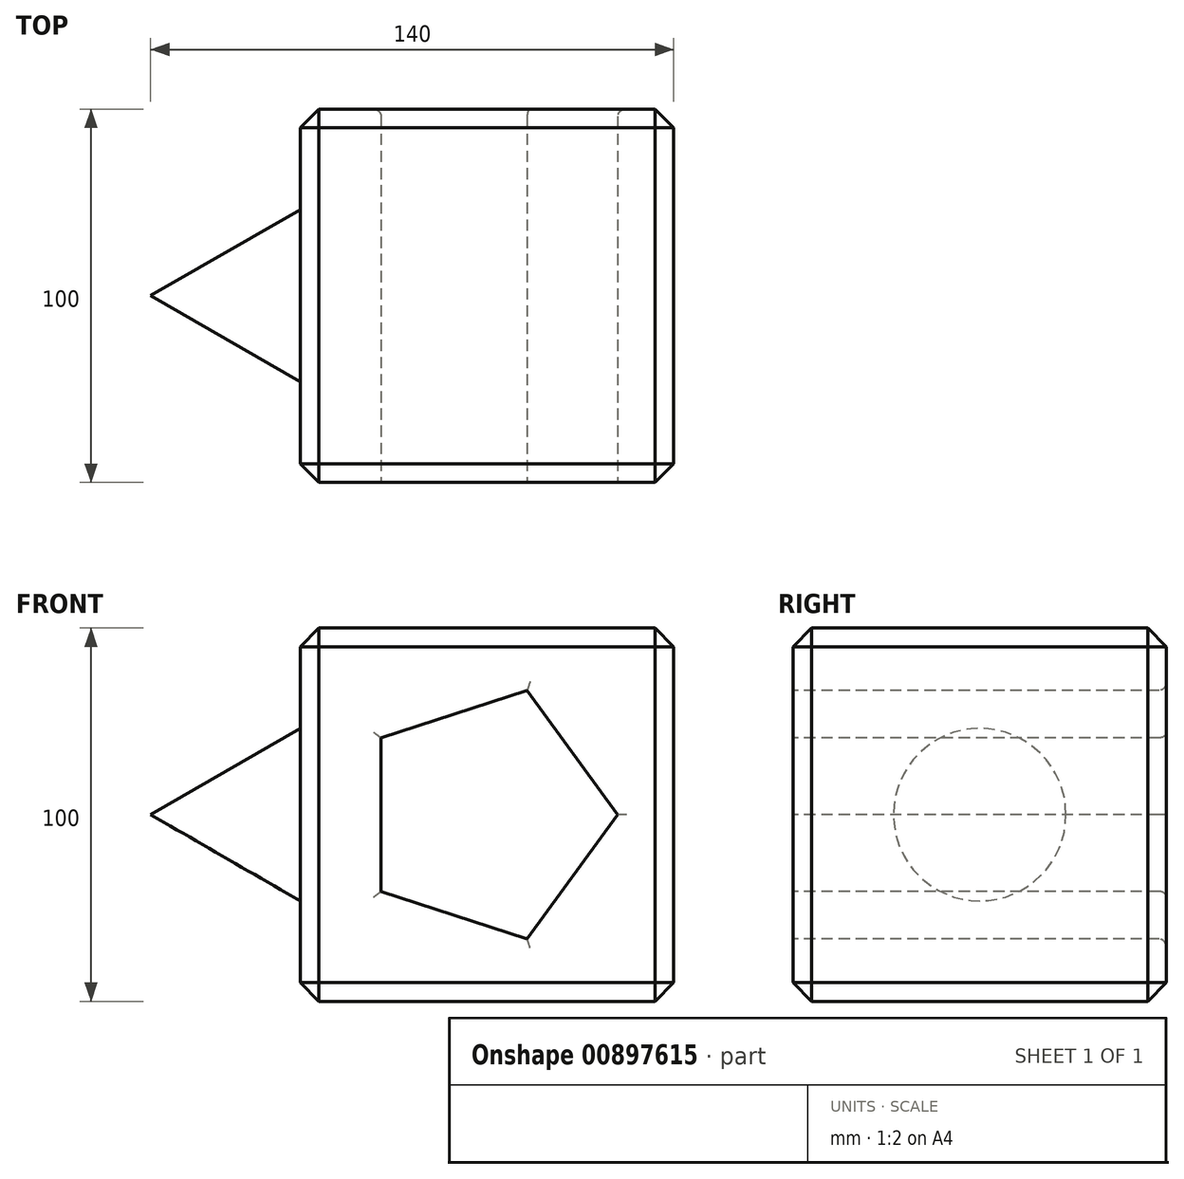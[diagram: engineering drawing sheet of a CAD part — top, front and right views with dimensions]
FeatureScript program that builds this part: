
annotation { "Feature Type Name" : "Feature", "Feature Type Description" : "" }
export const myFeature = defineFeature(function(context is Context, id is Id, definition is map)
    precondition{}
    {
        {
            var Q0;
            Q0=qCreatedBy(makeId("Front.planeOp"),FACE);
            var sketch = newSketch(context, id + "F0", { "sketchPlane" : qUnion([Q0])});
            skLineSegment(sketch, "E0.bottom", {"start": v(50, 50) * mm, "end": v(-50, 50) * mm});
            skLineSegment(sketch, "E0.top", {"start": v(50, -50) * mm, "end": v(-50, -50) * mm});
            skLineSegment(sketch, "E0.left", {"start": v(50, 50) * mm, "end": v(50, -50) * mm});
            skLineSegment(sketch, "E0.right", {"start": v(-50, 50) * mm, "end": v(-50, -50) * mm});
            skPoint(sketch, "E0.middle", {"position": v(0, 0) * mm});
            skSolve(sketch);
        }
        {
            var Q0;
            Q0 = qSketchRegion(id + "F0", true);
            extrude(context, id + "F1", {"entities" : qUnion([Q0]), "endBound" : BoundingType.SYMMETRIC, "depth" : 100 * mm, "offsetDistance" : 25 * mm});
        }
        {
            var Q0;
            Q0=makeQuery(id+"F1.opExtrude","CAP_FACE",FACE,{"disambiguationData":[OSD([sQuery(id+"F0.wireOp",EDGE,"E0.bottom"),sQuery(id+"F0.wireOp",EDGE,"E0.top"),sQuery(id+"F0.wireOp",EDGE,"E0.left"),sQuery(id+"F0.wireOp",EDGE,"E0.right")])],"isStart":false});
            var sketch = newSketch(context, id + "F2", { "sketchPlane" : qUnion([Q0])});
            skCircle(sketch, "E1.cCircle", {"center": v(0, 0) * mm, "radius": 35 * mm, "construction": true});
            skLineSegment(sketch, "E1.0", {"start": v(35, 0) * mm, "end": v(10.82, -33.29) * mm});
            skLineSegment(sketch, "E1.1", {"start": v(10.82, -33.29) * mm, "end": v(-28.32, -20.57) * mm});
            skLineSegment(sketch, "E1.2", {"start": v(-28.32, -20.57) * mm, "end": v(-28.32, 20.57) * mm});
            skLineSegment(sketch, "E1.3", {"start": v(-28.32, 20.57) * mm, "end": v(10.82, 33.29) * mm});
            skLineSegment(sketch, "E1.4", {"start": v(10.82, 33.29) * mm, "end": v(35, 0) * mm});
            skSolve(sketch);
        }
        {
            var Q0;
            Q0 = qSketchRegion(id + "F2", true);
            extrude(context, id + "F3", {"entities" : qUnion([Q0]), "operationType" : NewBodyOperationType.REMOVE, "oppositeDirection" : true, "depth" : 142.9 * mm, "offsetDistance" : 25 * mm});
        }
        {
            var Q0;
            Q0=makeQuery(id+"F1.opExtrude","SWEPT_FACE",FACE,{"disambiguationData":[OSD([sQuery(id+"F0.wireOp",EDGE,"E0.bottom")])]});
            var Q1;
            Q1=makeQuery(id+"F1.opExtrude","SWEPT_FACE",FACE,{"disambiguationData":[OSD([sQuery(id+"F0.wireOp",EDGE,"E0.left")])]});
            var Q2;
            Q2=makeQuery(id+"F1.opExtrude","SWEPT_FACE",FACE,{"disambiguationData":[OSD([sQuery(id+"F0.wireOp",EDGE,"E0.top")])]});
            var Q3;
            Q3=makeQuery(id+"F1.opExtrude","SWEPT_FACE",FACE,{"disambiguationData":[OSD([sQuery(id+"F0.wireOp",EDGE,"E0.right")])]});
            chamfer(context, id + "F4", {"entities" : qUnion([Q0, Q1, Q2, Q3]), "width" : 5 * mm, "tangentPropagation" : true});
        }
        {
            var Q0;
            Q0=makeQuery(id+"F3.boolean.opBoolean","INTERSECT",EDGE,{"derivedFrom":[makeQuery(id+"F1.opExtrude","CAP_FACE",FACE,{"disambiguationData":[OSD([sQuery(id+"F0.wireOp",EDGE,"E0.bottom"),sQuery(id+"F0.wireOp",EDGE,"E0.top"),sQuery(id+"F0.wireOp",EDGE,"E0.left"),sQuery(id+"F0.wireOp",EDGE,"E0.right")])],"isStart":true}),makeQuery(id+"F3.opExtrude","SWEPT_FACE",FACE,{"disambiguationData":[OSD([sQuery(id+"F2.wireOp",EDGE,"E1.0")])]})]});
            var Q1;
            Q1=makeQuery(id+"F3.boolean.opBoolean","INTERSECT",EDGE,{"derivedFrom":[makeQuery(id+"F1.opExtrude","CAP_FACE",FACE,{"disambiguationData":[OSD([sQuery(id+"F0.wireOp",EDGE,"E0.bottom"),sQuery(id+"F0.wireOp",EDGE,"E0.top"),sQuery(id+"F0.wireOp",EDGE,"E0.left"),sQuery(id+"F0.wireOp",EDGE,"E0.right")])],"isStart":true}),makeQuery(id+"F3.opExtrude","SWEPT_FACE",FACE,{"disambiguationData":[OSD([sQuery(id+"F2.wireOp",EDGE,"E1.1")])]})]});
            var Q2;
            Q2=makeQuery(id+"F3.boolean.opBoolean","INTERSECT",EDGE,{"derivedFrom":[makeQuery(id+"F1.opExtrude","CAP_FACE",FACE,{"disambiguationData":[OSD([sQuery(id+"F0.wireOp",EDGE,"E0.bottom"),sQuery(id+"F0.wireOp",EDGE,"E0.top"),sQuery(id+"F0.wireOp",EDGE,"E0.left"),sQuery(id+"F0.wireOp",EDGE,"E0.right")])],"isStart":true}),makeQuery(id+"F3.opExtrude","SWEPT_FACE",FACE,{"disambiguationData":[OSD([sQuery(id+"F2.wireOp",EDGE,"E1.2")])]})]});
            var Q3;
            Q3=makeQuery(id+"F3.boolean.opBoolean","INTERSECT",EDGE,{"derivedFrom":[makeQuery(id+"F1.opExtrude","CAP_FACE",FACE,{"disambiguationData":[OSD([sQuery(id+"F0.wireOp",EDGE,"E0.bottom"),sQuery(id+"F0.wireOp",EDGE,"E0.top"),sQuery(id+"F0.wireOp",EDGE,"E0.left"),sQuery(id+"F0.wireOp",EDGE,"E0.right")])],"isStart":true}),makeQuery(id+"F3.opExtrude","SWEPT_FACE",FACE,{"disambiguationData":[OSD([sQuery(id+"F2.wireOp",EDGE,"E1.3")])]})]});
            var Q4;
            Q4=makeQuery(id+"F3.boolean.opBoolean","INTERSECT",EDGE,{"derivedFrom":[makeQuery(id+"F1.opExtrude","CAP_FACE",FACE,{"disambiguationData":[OSD([sQuery(id+"F0.wireOp",EDGE,"E0.bottom"),sQuery(id+"F0.wireOp",EDGE,"E0.top"),sQuery(id+"F0.wireOp",EDGE,"E0.left"),sQuery(id+"F0.wireOp",EDGE,"E0.right")])],"isStart":true}),makeQuery(id+"F3.opExtrude","SWEPT_FACE",FACE,{"disambiguationData":[OSD([sQuery(id+"F2.wireOp",EDGE,"E1.4")])]})]});
            var Q5;
            Q5=makeQuery(id+"F3.boolean.opBoolean","COPY",EDGE,{"derivedFrom":makeQuery(id+"F3.opExtrude","CAP_EDGE",EDGE,{"disambiguationData":[OSD([sQuery(id+"F2.wireOp",EDGE,"E1.0")])],"isStart":true})});
            var Q6;
            Q6=makeQuery(id+"F3.boolean.opBoolean","COPY",EDGE,{"derivedFrom":makeQuery(id+"F3.opExtrude","CAP_EDGE",EDGE,{"disambiguationData":[OSD([sQuery(id+"F2.wireOp",EDGE,"E1.4")])],"isStart":true})});
            var Q7;
            Q7=makeQuery(id+"F3.boolean.opBoolean","COPY",EDGE,{"derivedFrom":makeQuery(id+"F3.opExtrude","CAP_EDGE",EDGE,{"disambiguationData":[OSD([sQuery(id+"F2.wireOp",EDGE,"E1.3")])],"isStart":true})});
            var Q8;
            Q8=makeQuery(id+"F3.boolean.opBoolean","COPY",EDGE,{"derivedFrom":makeQuery(id+"F3.opExtrude","CAP_EDGE",EDGE,{"disambiguationData":[OSD([sQuery(id+"F2.wireOp",EDGE,"E1.2")])],"isStart":true})});
            var Q9;
            Q9=makeQuery(id+"F3.boolean.opBoolean","COPY",EDGE,{"derivedFrom":makeQuery(id+"F3.opExtrude","CAP_EDGE",EDGE,{"disambiguationData":[OSD([sQuery(id+"F2.wireOp",EDGE,"E1.1")])],"isStart":true})});
            fillet(context, id + "F5", {"entities" : qUnion([Q0, Q1, Q2, Q3, Q4, Q5, Q6, Q7, Q8, Q9]), "radius" : 2 * mm, "tangentPropagation" : true, "allowEdgeOverflow" : false});
        }
        {
            var Q0;
            Q0=qCreatedBy(makeId("Top.planeOp"),FACE);
            var sketch = newSketch(context, id + "F6", { "sketchPlane" : qUnion([Q0])});
            skLineSegment(sketch, "E2", {"start": v(-50, 0) * mm, "end": v(-90, 0) * mm});
            skLineSegment(sketch, "E3", {"start": v(-90, 0) * mm, "end": v(-50, 23.1) * mm});
            skLineSegment(sketch, "E4", {"start": v(-50, 23.1) * mm, "end": v(-50, 0) * mm});
            skSolve(sketch);
        }
        {
            var Q0;
            Q0=makeQuery(id+"F6.imprint","IMPRINT",FACE,{"disambiguationData":[TD([[makeQuery(id+"F6.imprint","IMPRINT",EDGE,{"derivedFrom":sQuery(id+"F6.wireOp",EDGE,"E2")}),-1.0]])]});
            var Q1;
            Q1=sQuery(id+"F6.wireOp",EDGE,"E2");
            revolve(context, id + "F7", {"operationType" : NewBodyOperationType.ADD, "surfaceOperationType" : NewSurfaceOperationType.NEW, "entities" : qUnion([Q0]), "axis" : qUnion([Q1]), "revolveType" : RevolveType.FULL});
        }
    });
